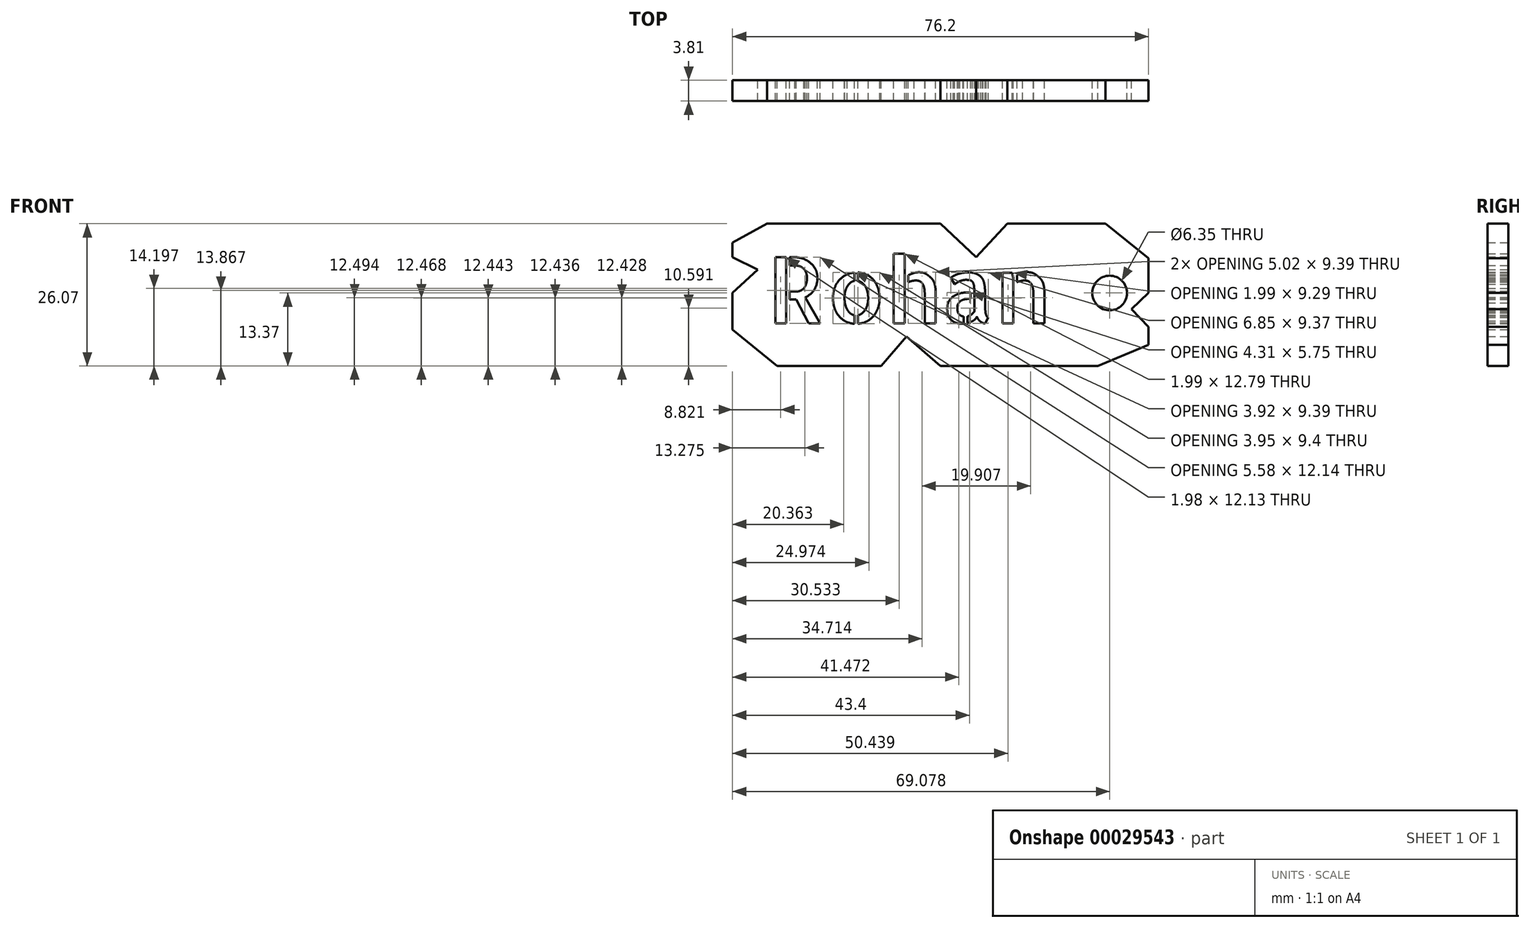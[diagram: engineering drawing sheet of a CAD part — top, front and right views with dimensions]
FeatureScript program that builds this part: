
annotation { "Feature Type Name" : "Feature", "Feature Type Description" : "" }
export const myFeature = defineFeature(function(context is Context, id is Id, definition is map)
    precondition{}
    {
        {
            var Q0;
            Q0=qCreatedBy(makeId("Front.planeOp"),FACE);
            var sketch = newSketch(context, id + "F0", { "sketchPlane" : qUnion([Q0])});
            skText(sketch, "E0", { "text": "Rohan", "fontName": "AllertaStencil-Regular.ttf"});
            skLineSegment(sketch, "E1", {"start": v(-59.17, 6.02) * mm, "end": v(-59.17, 12.7) * mm});
            skLineSegment(sketch, "E2", {"start": v(-59.17, 12.7) * mm, "end": v(-54.56, 17) * mm});
            skLineSegment(sketch, "E3", {"start": v(-59.17, 21.94) * mm, "end": v(-52.82, 25.4) * mm});
            skLineSegment(sketch, "E4", {"start": v(-54.56, 17) * mm, "end": v(-59.17, 19.28) * mm});
            skLineSegment(sketch, "E5", {"start": v(-59.17, 19.28) * mm, "end": v(-59.17, 21.94) * mm});
            skLineSegment(sketch, "E6", {"start": v(17, 3.22) * mm, "end": v(7.74, -0.67) * mm});
            skLineSegment(sketch, "E7", {"start": v(17.03, 12.7) * mm, "end": v(13.93, 9.71) * mm});
            skLineSegment(sketch, "E8", {"start": v(13.93, 9.71) * mm, "end": v(17, 6.52) * mm});
            skLineSegment(sketch, "E9", {"start": v(7.74, -0.67) * mm, "end": v(17, 3.22) * mm});
            skLineSegment(sketch, "E10", {"start": v(13.93, 9.71) * mm, "end": v(17.03, 12.7) * mm});
            skLineSegment(sketch, "E11.trimOffspring", {"start": v(17, 6.52) * mm, "end": v(17, 3.22) * mm});
            skLineSegment(sketch, "E12", {"start": v(-21.07, -0.67) * mm, "end": v(-27.32, 4.7) * mm});
            skLineSegment(sketch, "E13", {"start": v(-27.32, 4.7) * mm, "end": v(-31.94, -0.67) * mm});
            skLineSegment(sketch, "E14", {"start": v(-21.07, 25.4) * mm, "end": v(-14.52, 19.28) * mm});
            skLineSegment(sketch, "E15", {"start": v(-14.52, 19.28) * mm, "end": v(-8.8, 25.4) * mm});
            skLineSegment(sketch, "E16", {"start": v(9.13, 25.4) * mm, "end": v(17.03, 19.05) * mm});
            skLineSegment(sketch, "E17", {"start": v(-59.17, 6.02) * mm, "end": v(-50.97, -0.67) * mm});
            skLineSegment(sketch, "E18", {"start": v(17.03, 19.05) * mm, "end": v(17.03, 12.7) * mm});
            skLineSegment(sketch, "E19", {"start": v(-27.32, 4.7) * mm, "end": v(-21.07, -0.67) * mm});
            skLineSegment(sketch, "E20", {"start": v(-31.94, -0.67) * mm, "end": v(-50.97, -0.67) * mm});
            skLineSegment(sketch, "E21", {"start": v(-21.07, -0.67) * mm, "end": v(7.74, -0.67) * mm});
            skLineSegment(sketch, "E22", {"start": v(-21.07, 25.4) * mm, "end": v(-52.82, 25.4) * mm});
            skLineSegment(sketch, "E23", {"start": v(-8.8, 25.4) * mm, "end": v(9.13, 25.4) * mm});
            skCircle(sketch, "E24", {"center": v(9.9, 12.7) * mm, "radius": 3.18 * mm});
            const initialGuessF0  = {"E0": [-0.05282, 0.00713, 1, 0, 0.01214]};
            skSetInitialGuess(sketch, initialGuessF0);
            skSolve(sketch);
        }
        {
            var Q0;
            Q0=makeQuery(id+"F0.imprint","IMPRINT",FACE,{"disambiguationData":[TD([[makeQuery(id+"F0.imprint","IMPRINT",EDGE,{"derivedFrom":sQuery(id+"F0.wireOp",EDGE,"E0.sketch_text.stroke-0")}),1.0]])]});
            extrude(context, id + "F1", {"entities" : qUnion([Q0]), "depth" : 3.8 * mm});
        }
    });
